# Revit family: Projector_Screen-Draper_Inc-Ultimate_Access_E
name_source: partatom
category: Specialty Equipment
units: mm (PartAtom-declared; Revit-internal decimal feet)

## family parameters
Classification Number = 23.85.10.14.31
Cut with Voids When Loaded = No
Enable Cutting in Views = No
Host = Face
Maintain Annotation Orientation = No
Part Type = Normal
Room Calculation Point = No
Round Connector Dimension = Use Diameter
Shared = No

## types (1)
- NOT A TYPE - LOAD TYPE CATALOG
    Apparent Load = 132 VA
    Border = Yes
    Case Material = Paint - Draper - White
    Default Elevation = 4' - 0"
    Description = Projector Screen
    Frequency = 60 Hz
    Image Area = 42 1/2" x 56 1/2"
    Image Height = 3' - 6 1/2"
    Image Height Constraint = 3' - 6 1/2"
    Image Length = 4' - 8 1/2"
    Image Length Constraint = 4' - 8 1/2"
    Keynote = 10100
    Length = 6' - 4 3/8"
    Manufacturer = Draper Inc.
    Model = Ultimate Acess E
    Number of Poles = 1
    Overall Size = 46 1/2" x 59 1/2"
    Product Documentation Link = http://www.draperinc.com
    Product Name = Ultimate Access E
    Product Page URL = http://www.draperinc.com
    Projection Screen Material = Fabric - Draper - CH1900E - Pearl White
    Screen = 5' - 0 1/2"
    Screen Drop = 3' - 10 1/2"
    URL = http://www.draperinc.com
    Voltage = 110 V
    Width = 7 15/16"

## geometry (parser evidence)
native form markers: Blend x6, Sweep x3
no freeform markers — native parametric forms only
